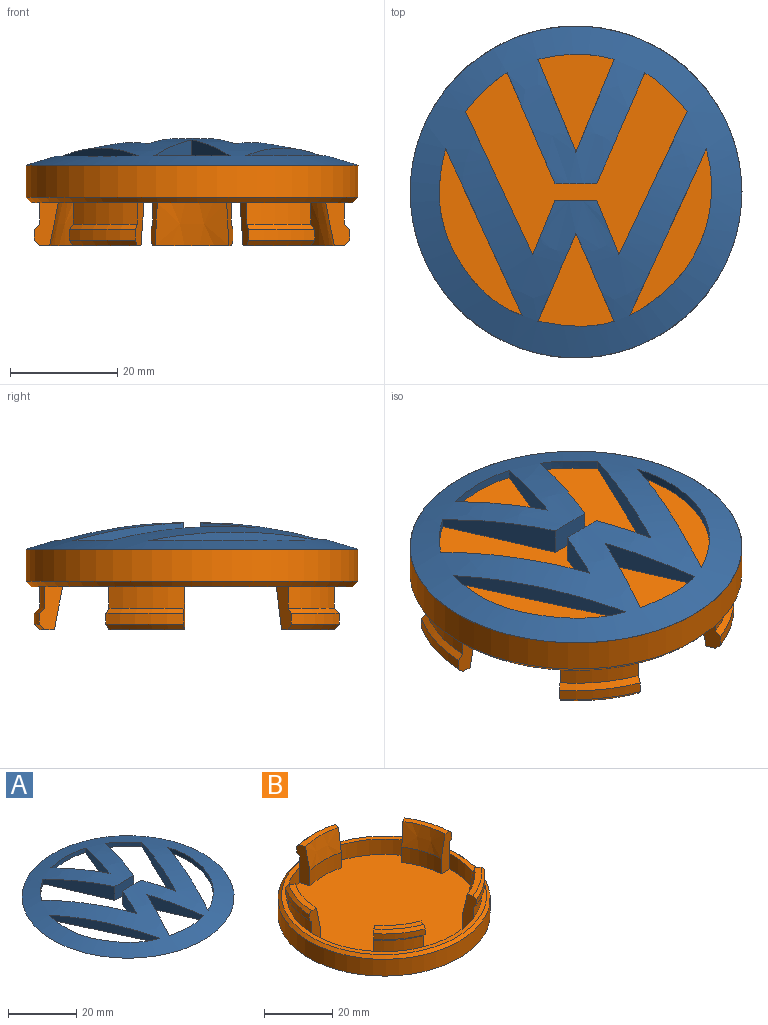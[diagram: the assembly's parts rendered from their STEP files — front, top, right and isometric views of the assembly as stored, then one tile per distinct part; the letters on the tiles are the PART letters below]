
ASSEMBLY  parts=2 mates=1
PART A: 22 faces, bbox 62x62x5 mm
  f0: plane 17.33x7.11mm, normal (0.93,0.38,0), area 64.7mm2, adj f1,f19,f20,f21
  f1: extruded ~14.23x1.57mm, area 22.6mm2, adj f0,f19,f20,f21
  f2: plane 26.8x12.58mm, normal (0.91,0.42,0), area 105.3mm2, adj f3,f15,f20,f21
  f3: extruded ~7.79x7.26mm, area 17.1mm2, adj f2,f4,f20,f21
  f4: plane 20.8x8.94mm, normal (-0.92,-0.39,0), area 83.6mm2, adj f3,f5,f20,f21
  f5: plane 7.8x4.99mm, normal (0,-1,0), area 38.7mm2, adj f4,f6,f20,f21
  f6: plane 20.74x8.99mm, normal (0.92,-0.4,0), area 83.6mm2, adj f5,f7,f20,f21
  f7: extruded ~7.9x7.2mm, area 17.2mm2, adj f6,f8,f20,f21
  f8: plane 26.8x12.73mm, normal (-0.9,0.43,0), area 105.3mm2, adj f7,f9,f20,f21
  f9: plane 10.12x4.91mm, normal (0.93,0.38,0), area 49.7mm2, adj f8,f10,f20,f21
  f10: plane 7.8x4.99mm, normal (0,1,0), area 38.7mm2, adj f9,f15,f20,f21
  f11: extruded ~31.1x15.48mm, area 63mm2, adj f16,f20,f21
  f12: extruded ~14.23x1.74mm, area 25mm2, adj f13,f17,f20,f21
  f13: plane 16.39x7.11mm, normal (0.92,-0.4,0), area 62.5mm2, adj f12,f17,f20,f21
  f14: plane 31.1x14.33mm, normal (0.91,-0.42,0), area 92.3mm2, adj f18,f20,f21
  f15: plane 10.12x4.91mm, normal (-0.93,0.38,0), area 49.7mm2, adj f2,f10,f20,f21
  f16: plane 31.1x14.3mm, normal (-0.91,-0.42,0), area 92.1mm2, adj f11,f20,f21
  f17: plane 16.39x7.12mm, normal (-0.92,-0.4,0), area 62.5mm2, adj f12,f13,f20,f21
  f18: extruded ~31.1x15.32mm, area 62.4mm2, adj f14,f20,f21
  f19: plane 17.33x7.12mm, normal (-0.92,0.38,0), area 64.7mm2, adj f0,f1,f20,f21
  f20: plane 62x62mm, normal (0,0,-1), area 1905.4mm2, adj f0,f1,f2,f3,f4,f5,f6,f7
  f21: sphere r=98.6mm, area 1961.9mm2, adj f0,f1,f2,f3,f4,f5,f6,f7
PART B: 55 faces, bbox 62x62x15 mm
  f0: plane 60x60mm, normal (0,0,1), area 275.7mm2, adj f4,f6,f9,f12,f15,f44,f46,f48
  f1: cylinder r=31mm len=62mm, axis (0,0,-1), area 1168.7mm2, adj f2,f54
  f2: plane 62x62mm, normal (0,0,-1), area 3019.1mm2, adj f1
  f3: plane 13.5x4.35mm, normal (0.97,-0.26,0), area 43.8mm2, adj f4,f19,f24,f31,f37,f42,f43,f52
  f4: cylinder r=28.5mm len=14.75mm, axis (0,0,-1), area 59.7mm2, adj f0,f3,f5,f37
  f5: plane 13.5x4.35mm, normal (-0.97,-0.26,0), area 43.8mm2, adj f4,f19,f24,f31,f37,f42,f43,f44
  f6: cylinder r=28.5mm len=14.03mm, axis (0,0,-1), area 59.7mm2, adj f0,f7,f8,f36
  f7: plane 13.5x4.49mm, normal (-0.05,-1,0), area 43.9mm2, adj f6,f20,f25,f32,f36,f41,f45,f46
  f8: plane 13.5x3.77mm, normal (0.54,0.84,0), area 43.9mm2, adj f6,f20,f25,f32,f36,f41,f44,f45
  f9: cylinder r=28.5mm len=11.94mm, axis (0,0,-1), area 59.7mm2, adj f0,f10,f11,f35
  f10: plane 13.5x4.2mm, normal (0.93,-0.36,0), area 43.9mm2, adj f9,f21,f26,f28,f35,f38,f47,f48
  f11: plane 13.5x3.5mm, normal (-0.63,0.78,0), area 43.8mm2, adj f9,f21,f26,f28,f35,f38,f46,f47
  f12: cylinder r=28.5mm len=11.94mm, axis (0,0,-1), area 59.7mm2, adj f0,f13,f14,f34
  f13: plane 13.5x3.5mm, normal (0.63,0.78,0), area 43.8mm2, adj f12,f22,f27,f29,f34,f39,f49,f50
  f14: plane 13.5x4.2mm, normal (-0.93,-0.36,0), area 43.8mm2, adj f12,f22,f27,f29,f34,f39,f48,f49
  f15: cylinder r=28.5mm len=14.03mm, axis (0,0,-1), area 59.7mm2, adj f0,f16,f17,f33
  f16: plane 13.5x3.77mm, normal (-0.54,0.84,0), area 43.8mm2, adj f15,f18,f23,f30,f33,f40,f51,f52
  f17: plane 13.5x4.49mm, normal (0.05,-1,0), area 43.8mm2, adj f15,f18,f23,f30,f33,f40,f50,f51
  f18: plane 14.13x6.15mm, normal (0,0,1), area 27.4mm2, adj f16,f17,f30,f40
  f19: plane 14.75x2.81mm, normal (0,0,1), area 27.4mm2, adj f3,f5,f31,f42
  f20: plane 14.13x6.15mm, normal (0,0,1), area 27.4mm2, adj f7,f8,f32,f41
  f21: plane 12.62x9.87mm, normal (0,0,1), area 27.4mm2, adj f10,f11,f28,f38
  f22: plane 12.62x9.87mm, normal (0,0,1), area 27.4mm2, adj f13,f14,f29,f39
  f23: cylinder r=29.5mm len=14.52mm, axis (0,0,-1), area 30.9mm2, adj f16,f17,f30,f33
  f24: cylinder r=29.5mm len=15.27mm, axis (0,0,-1), area 30.9mm2, adj f3,f5,f31,f37
  f25: cylinder r=29.5mm len=14.52mm, axis (0,0,-1), area 30.9mm2, adj f7,f8,f32,f36
  f26: cylinder r=29.5mm len=12.35mm, axis (0,0,-1), area 30.9mm2, adj f10,f11,f28,f35
  f27: cylinder r=29.5mm len=12.35mm, axis (0,0,-1), area 30.9mm2, adj f13,f14,f29,f34
  f28: cone r=28.5mm half-angle=45deg, axis (0,0,-1), area 21.5mm2, adj f10,f11,f21,f26
  f29: cone r=28.5mm half-angle=45deg, axis (0,0,-1), area 21.5mm2, adj f13,f14,f22,f27
  f30: cone r=28.5mm half-angle=45deg, axis (0,0,-1), area 21.5mm2, adj f16,f17,f18,f23
  f31: cone r=28.5mm half-angle=45deg, axis (0,0,-1), area 21.5mm2, adj f3,f5,f19,f24
  f32: cone r=28.5mm half-angle=45deg, axis (0,0,-1), area 21.5mm2, adj f7,f8,f20,f25
  f33: cone r=29.5mm half-angle=45deg, axis (0,0,1), area 21.5mm2, adj f15,f16,f17,f23
  f34: cone r=29.5mm half-angle=45deg, axis (0,0,1), area 21.5mm2, adj f12,f13,f14,f27
  f35: cone r=29.5mm half-angle=45deg, axis (0,0,1), area 21.5mm2, adj f9,f10,f11,f26
  f36: cone r=29.5mm half-angle=45deg, axis (0,0,1), area 21.5mm2, adj f6,f7,f8,f25
  f37: cone r=29.5mm half-angle=45deg, axis (0,0,1), area 21.5mm2, adj f3,f4,f5,f24
  f38: cone r=25mm half-angle=11.3deg, axis (0,0,1), area 110.2mm2, adj f10,f11,f21,f47
  f39: cone r=25mm half-angle=11.3deg, axis (0,0,1), area 110.2mm2, adj f13,f14,f22,f49
  f40: cone r=25mm half-angle=11.3deg, axis (0,0,1), area 110.2mm2, adj f16,f17,f18,f51
  f41: cone r=25mm half-angle=11.3deg, axis (0,0,1), area 110.2mm2, adj f7,f8,f20,f45
  f42: cone r=25mm half-angle=11.3deg, axis (0,0,1), area 110.2mm2, adj f3,f5,f19,f43
  f43: cylinder r=25mm len=12.94mm, axis (0,0,1), area 72mm2, adj f3,f5,f42,f53
  f44: cylinder r=28.5mm len=16.53mm, axis (0,0,1), area 114.9mm2, adj f0,f5,f8,f53
  f45: cylinder r=25mm len=12.31mm, axis (0,0,1), area 72mm2, adj f7,f8,f41,f53
  f46: cylinder r=28.5mm len=19.43mm, axis (0,0,1), area 114.9mm2, adj f0,f7,f11,f53
  f47: cylinder r=25mm len=10.47mm, axis (0,0,1), area 72mm2, adj f10,f11,f38,f53
  f48: cylinder r=28.5mm len=20.43mm, axis (0,0,1), area 114.9mm2, adj f0,f10,f14,f53
  f49: cylinder r=25mm len=10.47mm, axis (0,0,1), area 72mm2, adj f13,f14,f39,f53
  f50: cylinder r=28.5mm len=19.43mm, axis (0,0,1), area 114.9mm2, adj f0,f13,f17,f53
  f51: cylinder r=25mm len=12.31mm, axis (0,0,1), area 72mm2, adj f16,f17,f40,f53
  f52: cylinder r=28.5mm len=16.53mm, axis (0,0,1), area 114.9mm2, adj f0,f3,f16,f53
  f53: plane 57x56.03mm, normal (0,0,1), area 2306.6mm2, adj f3,f5,f7,f8,f10,f11,f13,f14
  f54: cone r=30mm half-angle=45deg, axis (0,0,-1), area 271mm2, adj f0,f1
PLACE A t=(-32.12,51.23,-0.93)mm
PLACE B rot(axis=(0,1,0),180deg) t=(-61.8,43.09,-0.93)mm
MATE fastened B.f1 <-> A.f20  axis (0,0,1) through (-31.26,51.07,-0.93)mm
